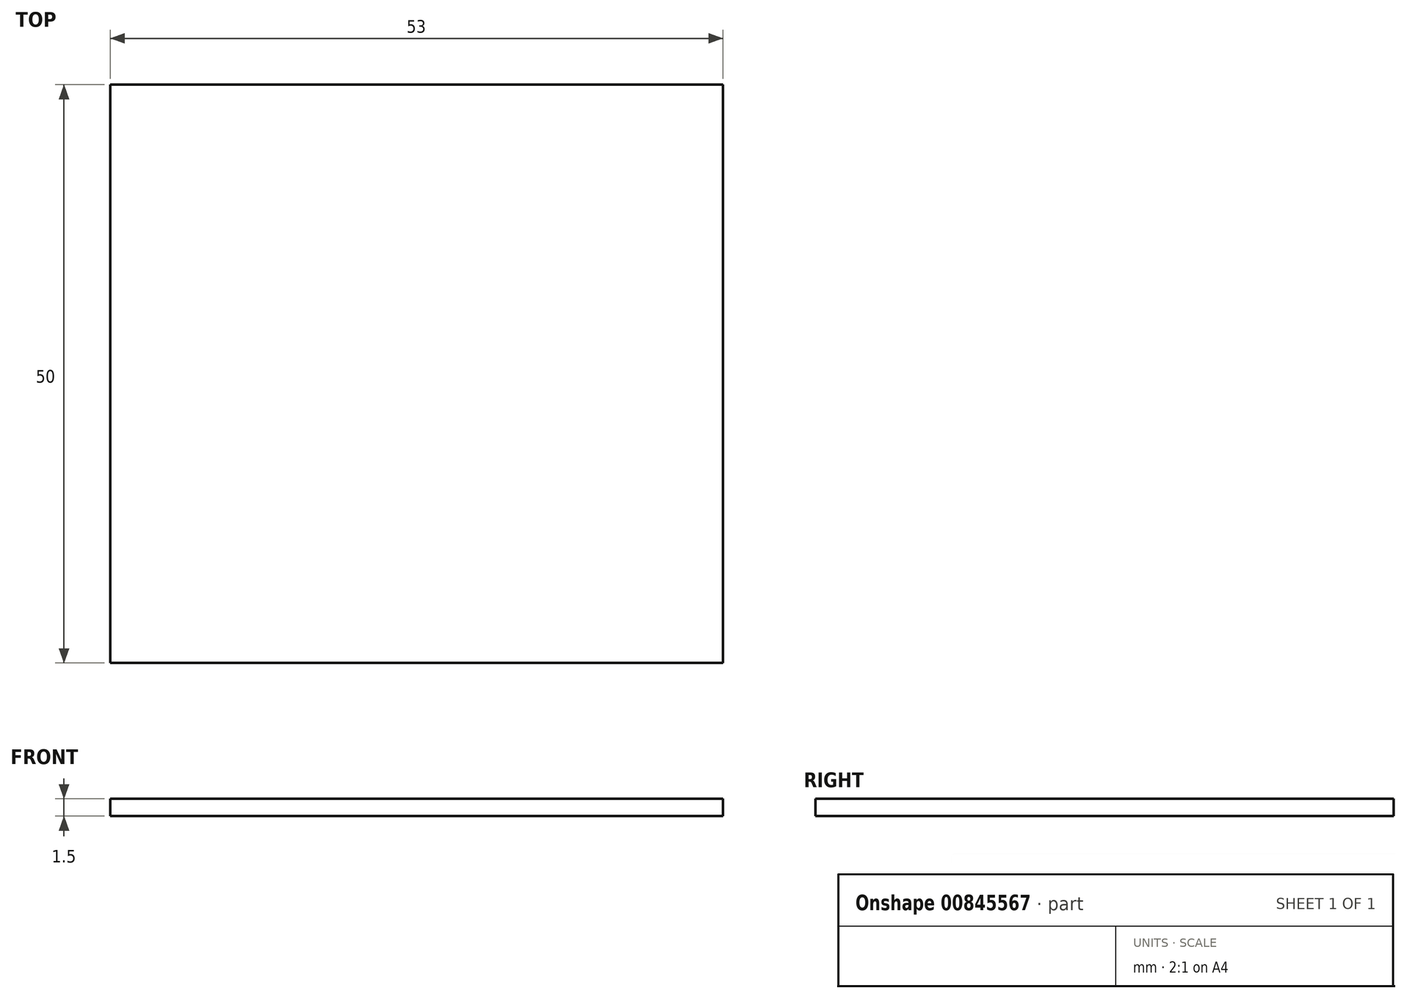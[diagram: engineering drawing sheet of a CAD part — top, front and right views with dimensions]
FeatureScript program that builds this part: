
annotation { "Feature Type Name" : "Feature", "Feature Type Description" : "" }
export const myFeature = defineFeature(function(context is Context, id is Id, definition is map)
    precondition{}
    {
        {
            var Q0;
            Q0=qCreatedBy(makeId("Top.planeOp"),FACE);
            var sketch = newSketch(context, id + "F0", { "sketchPlane" : qUnion([Q0])});
            skLineSegment(sketch, "E0.bottom", {"start": v(-26.5, -25) * mm, "end": v(26.5, -25) * mm});
            skLineSegment(sketch, "E0.top", {"start": v(-26.5, 25) * mm, "end": v(26.5, 25) * mm});
            skLineSegment(sketch, "E0.left", {"start": v(-26.5, -25) * mm, "end": v(-26.5, 25) * mm});
            skLineSegment(sketch, "E0.right", {"start": v(26.5, -25) * mm, "end": v(26.5, 25) * mm});
            skPoint(sketch, "E0.middle", {"position": v(0, 0) * mm});
            skSolve(sketch);
        }
        {
            var Q0;
            Q0=makeQuery(id+"F0.imprint","IMPRINT",FACE,{"disambiguationData":[TD([[makeQuery(id+"F0.imprint","IMPRINT",EDGE,{"derivedFrom":sQuery(id+"F0.wireOp",EDGE,"E0.bottom")}),1.0]])]});
            extrude(context, id + "F1", {"entities" : qUnion([Q0]), "depth" : 1.5 * mm, "offsetDistance" : 25 * mm});
        }
    });
